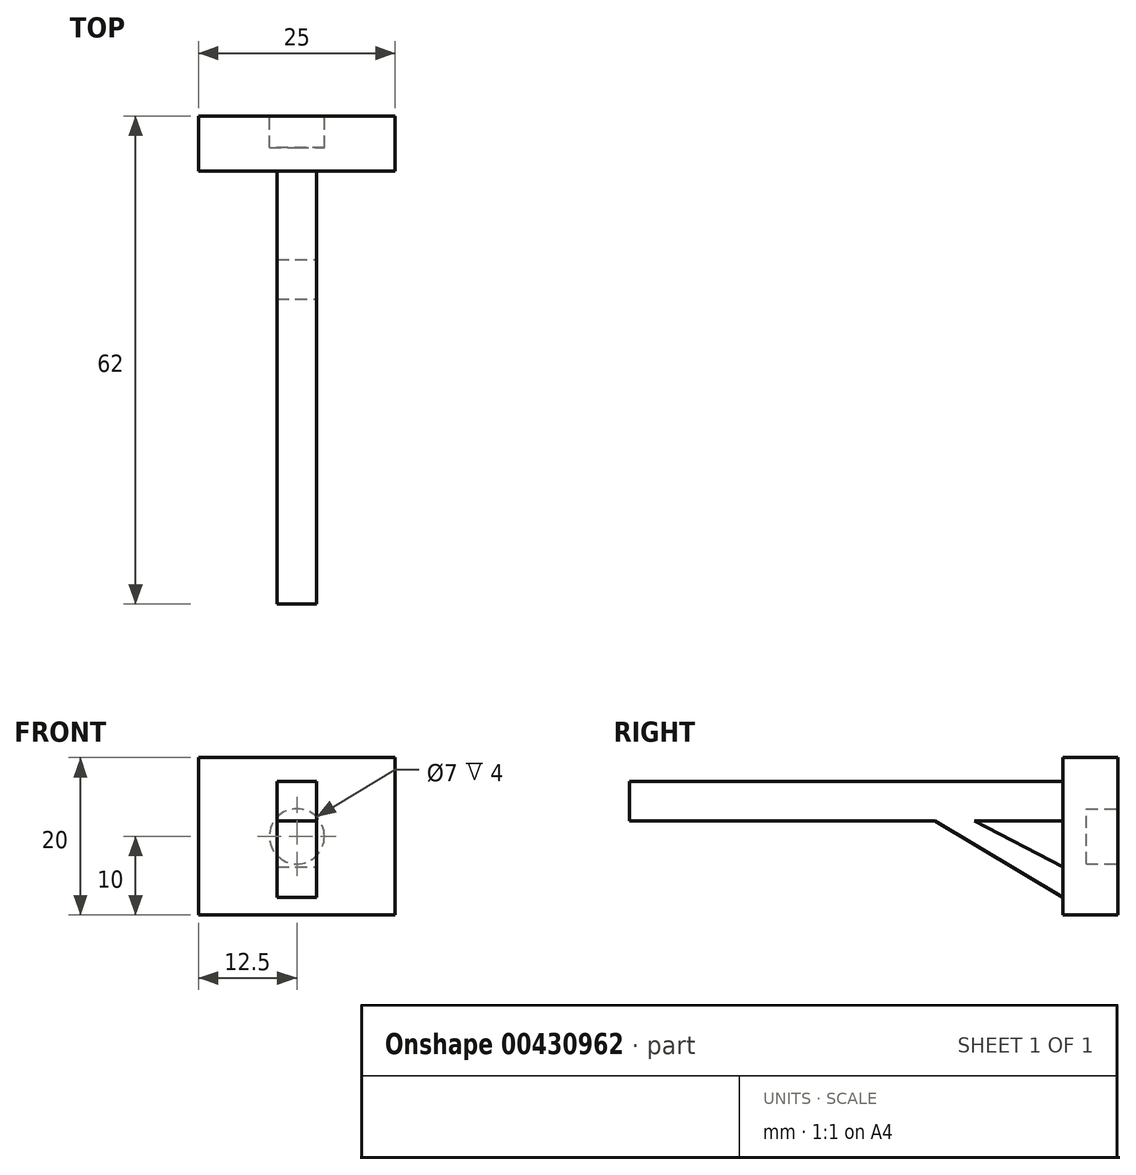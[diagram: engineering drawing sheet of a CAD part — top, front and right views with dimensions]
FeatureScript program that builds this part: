
annotation { "Feature Type Name" : "Feature", "Feature Type Description" : "" }
export const myFeature = defineFeature(function(context is Context, id is Id, definition is map)
    precondition{}
    {
        {
            var Q0;
            Q0=qCreatedBy(makeId("Front.planeOp"),FACE);
            var sketch = newSketch(context, id + "F0", { "sketchPlane" : qUnion([Q0])});
            skLineSegment(sketch, "E0.top", {"start": v(0, 10) * mm, "end": v(-12.5, 10) * mm});
            skLineSegment(sketch, "E0.right", {"start": v(-12.5, 0.04) * mm, "end": v(-12.5, 10) * mm});
            skLineSegment(sketch, "E1.bottom", {"start": v(-12.5, 10) * mm, "end": v(12.5, 10) * mm});
            skLineSegment(sketch, "E1.top", {"start": v(-12.5, -10) * mm, "end": v(12.5, -10) * mm});
            skLineSegment(sketch, "E1.left", {"start": v(-12.5, 10) * mm, "end": v(-12.5, -10) * mm});
            skLineSegment(sketch, "E1.right", {"start": v(12.5, 10) * mm, "end": v(12.5, -10) * mm});
            skPoint(sketch, "E1.middle", {"position": v(0, 0) * mm});
            skSolve(sketch);
        }
        {
            var Q0;
            {var subQ4=sQuery(id+"F0.wireOp",EDGE,"E1.top");Q0=makeQuery(id+"F0.imprint","IMPRINT",FACE,{"disambiguationData":[TD([[makeQuery(id+"F0.imprint","IMPRINT",EDGE,{"derivedFrom":subQ4}),1.0]])]});}
            extrude(context, id + "F1", {"entities" : qUnion([Q0]), "depth" : 7 * mm});
        }
        {
            var Q0;
            Q0=qCreatedBy(makeId("Front.planeOp"),FACE);
            var sketch = newSketch(context, id + "F2", { "sketchPlane" : qUnion([Q0])});
            skCircle(sketch, "E2", {"center": v(0, 0) * mm, "radius": 3.5 * mm});
            skSolve(sketch);
        }
        {
            var Q0;
            Q0=makeQuery(id+"F2.imprint","IMPRINT",FACE,{"disambiguationData":[TD([[makeQuery(id+"F2.imprint","IMPRINT",EDGE,{"derivedFrom":sQuery(id+"F2.wireOp",EDGE,"E2")}),1.0]])]});
            extrude(context, id + "F3", {"entities" : qUnion([Q0]), "operationType" : NewBodyOperationType.REMOVE, "depth" : 4 * mm});
        }
        {
            var Q0;
            Q0=makeQuery(id+"F1.opExtrude","CAP_FACE",FACE,{"disambiguationData":[OSD([sQuery(id+"F0.wireOp",EDGE,"E1.bottom"),sQuery(id+"F0.wireOp",EDGE,"E1.top"),sQuery(id+"F0.wireOp",EDGE,"E1.left"),sQuery(id+"F0.wireOp",EDGE,"E1.right")])],"isStart":false});
            var sketch = newSketch(context, id + "F4", { "sketchPlane" : qUnion([Q0])});
            skLineSegment(sketch, "E3", {"start": v(0, 6.95) * mm, "end": v(-2.5, 6.95) * mm});
            skLineSegment(sketch, "E4", {"start": v(-2.5, 6.95) * mm, "end": v(-2.5, 1.95) * mm});
            skLineSegment(sketch, "E5", {"start": v(-2.5, 1.95) * mm, "end": v(2.5, 1.95) * mm});
            skLineSegment(sketch, "E6", {"start": v(2.5, 1.95) * mm, "end": v(2.5, 6.95) * mm});
            skLineSegment(sketch, "E7", {"start": v(2.5, 6.95) * mm, "end": v(0, 6.95) * mm});
            skSolve(sketch);
        }
        {
            var Q0;
            Q0=makeQuery(id+"F4.imprint","IMPRINT",FACE,{"disambiguationData":[TD([[makeQuery(id+"F4.imprint","IMPRINT",EDGE,{"derivedFrom":sQuery(id+"F4.wireOp",EDGE,"E3")}),1.0]])]});
            extrude(context, id + "F5", {"entities" : qUnion([Q0]), "operationType" : NewBodyOperationType.ADD, "depth" : 55 * mm});
        }
        {
            var Q0;
            Q0=makeQuery(id+"F5.opExtrude","SWEPT_FACE",FACE,{"disambiguationData":[OSD([sQuery(id+"F4.wireOp",EDGE,"E6")])]});
            var sketch = newSketch(context, id + "F6", { "sketchPlane" : qUnion([Q0])});
            skLineSegment(sketch, "E8", {"start": v(-18.23, 1.95) * mm, "end": v(-5.5, -4.65) * mm});
            skLineSegment(sketch, "E9", {"start": v(-23.23, 1.95) * mm, "end": v(-18.23, 1.95) * mm});
            skLineSegment(sketch, "E10", {"start": v(-5.5, -4.65) * mm, "end": v(-5.5, -8.65) * mm});
            skLineSegment(sketch, "E11", {"start": v(-23.23, 1.95) * mm, "end": v(-5.5, -8.65) * mm});
            skSolve(sketch);
        }
        {
            var Q0;
            Q0=makeQuery(id+"F6.imprint","IMPRINT",FACE,{"disambiguationData":[TD([[makeQuery(id+"F6.imprint","IMPRINT",EDGE,{"derivedFrom":sQuery(id+"F6.wireOp",EDGE,"E8")}),-1.0]])]});
            extrude(context, id + "F7", {"entities" : qUnion([Q0]), "operationType" : NewBodyOperationType.ADD, "oppositeDirection" : true, "depth" : 5 * mm});
        }
    });
